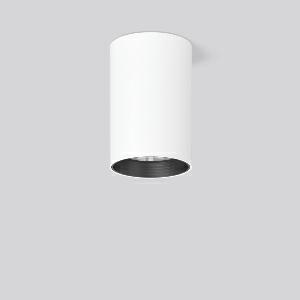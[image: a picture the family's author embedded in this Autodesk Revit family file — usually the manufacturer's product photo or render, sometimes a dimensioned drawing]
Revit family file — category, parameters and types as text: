
# Revit family: heledon_maxi_a_931227_002_3_76_f1a0
name_source: partatom
category: Lighting Fixtures
units: mm (PartAtom-declared; Revit-internal decimal feet)

## family parameters
Cut with Voids When Loaded = No
Host = Face
Light Source = No
Part Type = Normal
Room Calculation Point = No
Round Connector Dimension = Use Diameter
Shared = No

## types (1)
- HELEDON maxi A (1 x LED Modul 935, 3750 lm, 3500)
    Apparent Load = 35 VA
    Approval mark = CE
    CIE Flux Codes = 97 100 100 100 100
    Color Rendering = 92
    Color Temperature = 3500
    Default Elevation = 1800 mm
    Description = Series: HELEDON maxi
Cylindrical surface-mounted downlight. Housing: die-cast aluminium, powder-coated. Internal ceiling frame polycarbonate with bayonet mounting. Black plastic ring and recessed LED to prevent glare from the side. Optical assembly with lens made of plastic (polycarbonate) for the best homogeneous light distribution - can be changed without tools. Best colour rendering index Ra>90. Suitable for Ceiling mounting. Easy installation with a separate ceiling frame with bayonet mounting and plug connection. Driver integrated. Connected via plug-in connector. High quality converter without flickering and stroboscopic effect. The following accessories can be mounted without use of tools: interchangeable lenses, decorative glasses, honeycomb louvre, clear and frosted diffusers, white interchangeable plastic ring. 
Colour: traffic white, matt (RAL 9016)
Diameter: 123 mm
Height: 183 mm
Lamp: LED
Socket: without socket
Colour temperature: 3500K
Colour rendering index (CRI): 92
System power: 35 W
Rated luminous flux: 3750 lm
Luminous efficiency: 107 lm/W
Control gear: Converter, dimmable, DALI
Protection class: I
Type of protection: IP 20
    Height = 183 mm
    Lamp = 1 x LED Modul 935
    Lamp Light Flux = 3750 lm
    Lamp count = 1
    Length = 123 mm
    Lifetime = 50000 h
    Luminous efficacy = 107 lm/W
    Manufacturer = RZB
    ModVariant = No
    Model = 931227.002.3.76
    Mounting Place = Ceiling
    Mounting Type = Surface mounted
    Number of Poles = 1
    OnlyDefault = Yes
    Power Factor = 1
    Product Name = HELEDON maxi A
    Product group = Surface mounted downlights
    ProductGroupID = 302
    Protection Class = Protection class I
    Protection Degree = IP 20
    RLX_Detail_Level = 1
    RLX_Emergency_Light_Flux = 0 lm
    RLX_Emergency_Type = 0
    RLX_Emergency_Type_DB = No
    RlxData = <blob elided: 100353 chars, md5=f9fc1197>
    Socket = socket
    Standby Power = 0 W
    System Light Flux = 3750 lm
    System Power = 35 W
    Type Comments = Product without accessories
    Type Image = 931193.002.jpg
    URL = http://relux.com
    VarID = ---
    Voltage = 230 V
    Voltage Range = 220-240 V
    Weight = 0.00 kg
    Width = 0 mm  [stored 0 ft]

note: [stored X ft] marks values corroborated as IEEE doubles in the binary element streams (Revit-internal decimal feet)

## geometry (parser evidence)
native form markers: Blend x4, Sweep x11
no freeform markers — native parametric forms only
